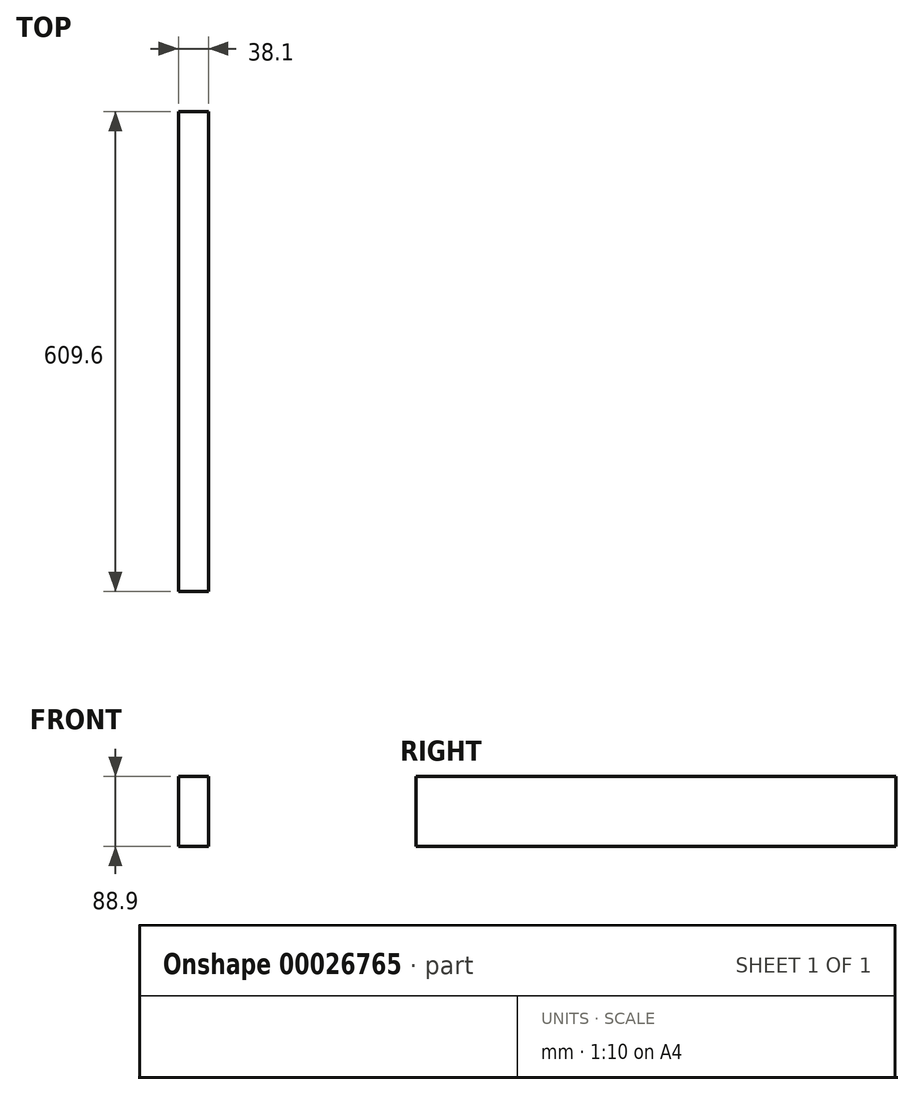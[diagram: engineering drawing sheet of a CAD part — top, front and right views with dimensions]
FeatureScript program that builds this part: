
annotation { "Feature Type Name" : "Feature", "Feature Type Description" : "" }
export const myFeature = defineFeature(function(context is Context, id is Id, definition is map)
    precondition{}
    {
        {
            var Q0;
            Q0=qCreatedBy(makeId("Front.planeOp"),FACE);
            var sketch = newSketch(context, id + "F0", { "sketchPlane" : qUnion([Q0])});
            skLineSegment(sketch, "E0.rect.bottom", {"start": v(-19.05, 44.45) * mm, "end": v(19.05, 44.45) * mm});
            skLineSegment(sketch, "E0.rect.top", {"start": v(-19.05, -44.45) * mm, "end": v(19.05, -44.45) * mm});
            skLineSegment(sketch, "E0.rect.left", {"start": v(-19.05, 44.45) * mm, "end": v(-19.05, -44.45) * mm});
            skLineSegment(sketch, "E0.rect.right", {"start": v(19.05, 44.45) * mm, "end": v(19.05, -44.45) * mm});
            skPoint(sketch, "E0.rect.middle", {"position": v(0, 0) * mm});
            skSolve(sketch);
        }
        {
            var Q0;
            Q0 = qSketchRegion(id + "F0", true);
            extrude(context, id + "F1", {"entities" : qUnion([Q0]), "depth" : 609.6 * mm});
        }
    });
